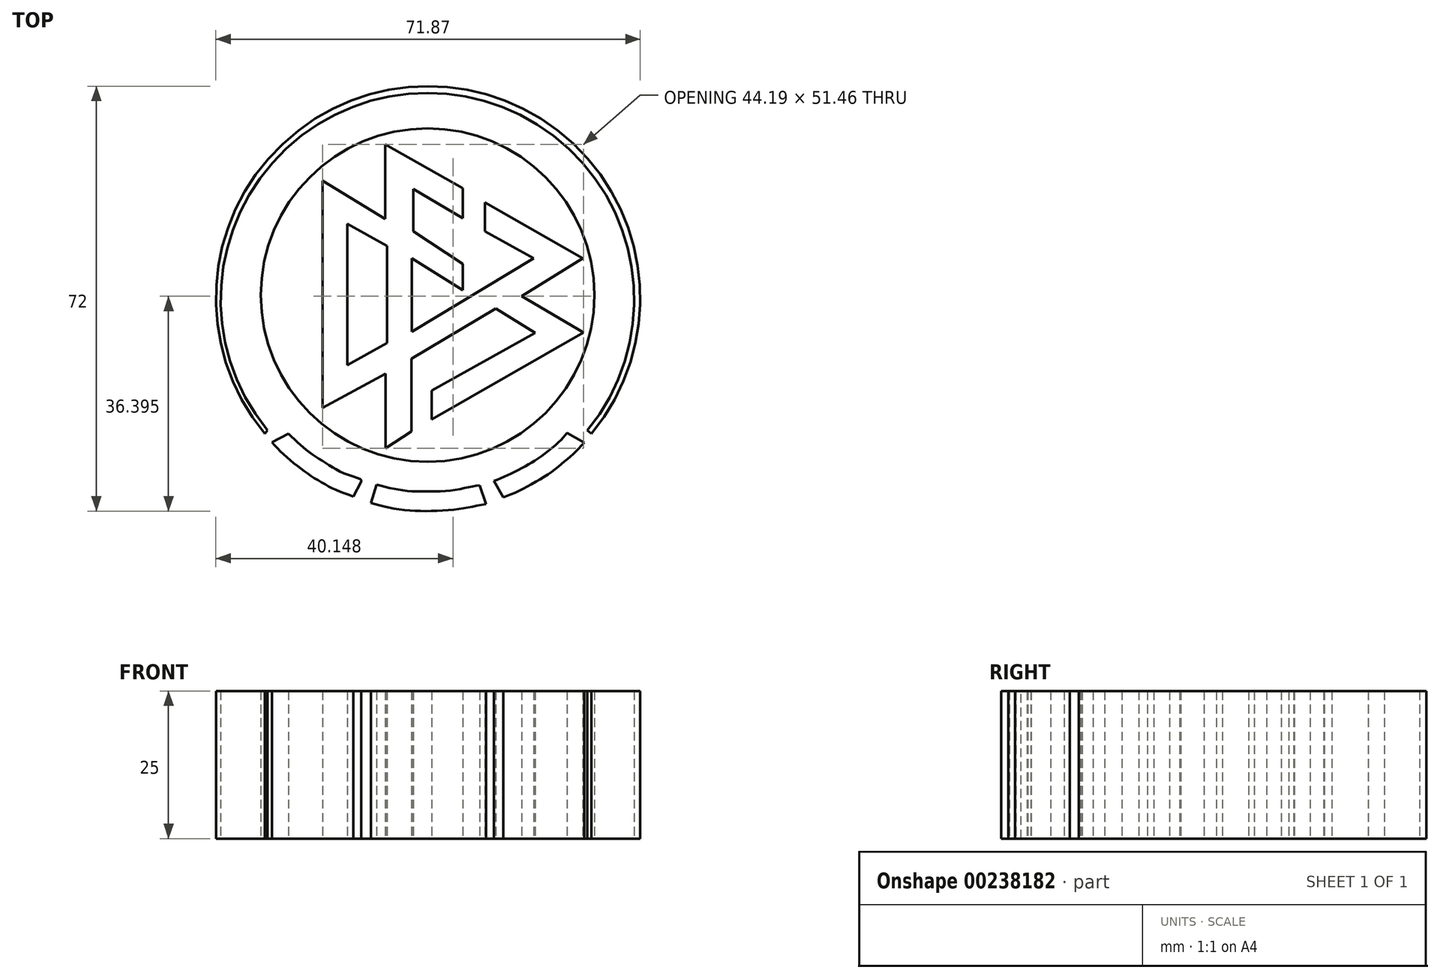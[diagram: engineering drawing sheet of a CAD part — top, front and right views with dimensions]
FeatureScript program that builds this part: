
annotation { "Feature Type Name" : "Feature", "Feature Type Description" : "" }
export const myFeature = defineFeature(function(context is Context, id is Id, definition is map)
    precondition{}
    {
        {
            var Q0;
            Q0=qCreatedBy(makeId("Top.planeOp"),FACE);
            var sketch = newSketch(context, id + "F0", { "sketchPlane" : qUnion([Q0])});
            skLineSegment(sketch, "E0", {"start": v(53.13, 37.91) * mm, "end": v(63.6, 31.78) * mm});
            skLineSegment(sketch, "E1", {"start": v(53.13, 37.91) * mm, "end": v(63.53, 44.34) * mm});
            skLineSegment(sketch, "E2", {"start": v(63.53, 44.34) * mm, "end": v(46.93, 53.84) * mm});
            skLineSegment(sketch, "E3", {"start": v(46.93, 53.84) * mm, "end": v(46.93, 48.9) * mm});
            skLineSegment(sketch, "E4", {"start": v(46.93, 48.9) * mm, "end": v(55.15, 44.34) * mm});
            skLineSegment(sketch, "E5", {"start": v(55.15, 44.34) * mm, "end": v(34.52, 31.9) * mm});
            skLineSegment(sketch, "E6", {"start": v(34.52, 31.9) * mm, "end": v(34.52, 44.34) * mm});
            skLineSegment(sketch, "E7", {"start": v(34.52, 44.34) * mm, "end": v(43.2, 38.96) * mm});
            skLineSegment(sketch, "E8", {"start": v(43.2, 38.96) * mm, "end": v(43.2, 43.37) * mm});
            skLineSegment(sketch, "E9", {"start": v(43.2, 43.37) * mm, "end": v(34.82, 48.9) * mm});
            skLineSegment(sketch, "E10", {"start": v(34.82, 48.9) * mm, "end": v(34.82, 56.08) * mm});
            skLineSegment(sketch, "E11", {"start": v(34.82, 56.08) * mm, "end": v(43.2, 51.15) * mm});
            skLineSegment(sketch, "E12", {"start": v(43.2, 51.15) * mm, "end": v(43.2, 56.23) * mm});
            skLineSegment(sketch, "E13", {"start": v(43.2, 56.23) * mm, "end": v(30.03, 63.63) * mm});
            skLineSegment(sketch, "E14", {"start": v(30.03, 63.63) * mm, "end": v(30.03, 51) * mm});
            skLineSegment(sketch, "E15", {"start": v(30.03, 51) * mm, "end": v(19.41, 57.5) * mm});
            skLineSegment(sketch, "E16", {"start": v(23.6, 50.17) * mm, "end": v(23.6, 26.25) * mm});
            skLineSegment(sketch, "E17", {"start": v(23.6, 26.25) * mm, "end": v(30.33, 29.99) * mm});
            skLineSegment(sketch, "E18", {"start": v(30.33, 29.99) * mm, "end": v(30.33, 46.44) * mm});
            skLineSegment(sketch, "E19", {"start": v(30.33, 46.44) * mm, "end": v(23.6, 50.17) * mm});
            skLineSegment(sketch, "E20", {"start": v(19.41, 57.5) * mm, "end": v(19.41, 19.03) * mm});
            skLineSegment(sketch, "E21", {"start": v(19.41, 19.03) * mm, "end": v(30.13, 24.76) * mm});
            skLineSegment(sketch, "E22", {"start": v(30.13, 24.76) * mm, "end": v(30.13, 12.18) * mm});
            skLineSegment(sketch, "E23", {"start": v(30.13, 12.18) * mm, "end": v(34.5, 15.03) * mm});
            skLineSegment(sketch, "E24", {"start": v(34.5, 15.03) * mm, "end": v(34.5, 27.3) * mm});
            skLineSegment(sketch, "E25", {"start": v(34.5, 27.3) * mm, "end": v(48.78, 35.83) * mm});
            skLineSegment(sketch, "E26", {"start": v(48.78, 35.83) * mm, "end": v(55.45, 31.74) * mm});
            skLineSegment(sketch, "E27", {"start": v(55.45, 31.74) * mm, "end": v(37.93, 21.9) * mm});
            skLineSegment(sketch, "E28", {"start": v(37.93, 21.9) * mm, "end": v(37.93, 17.02) * mm});
            skLineSegment(sketch, "E29", {"start": v(37.93, 17.02) * mm, "end": v(63.6, 31.78) * mm});
            skCircle(sketch, "E30", {"center": v(37.22, 38.12) * mm, "radius": 28.25 * mm});
            skPoint(sketch, "E30.centerSnap0", {"position": v(34.52, 38.12) * mm});
            skArc(sketch, "E31", {"start": v(64.3, 15.18) * mm, "mid": v(37.22, 72.37) * mm, "end": v(10.07, 15.21) * mm});
            skArc(sketch, "E32", {"start": v(64.98, 14.66) * mm, "mid": v(37.27, 73.5) * mm, "end": v(9.65, 14.61) * mm});
            skLineSegment(sketch, "E33", {"start": v(9.65, 14.61) * mm, "end": v(10.07, 15.21) * mm});
            skLineSegment(sketch, "E34", {"start": v(64.3, 15.18) * mm, "end": v(64.98, 14.66) * mm});
            skLineSegment(sketch, "E35", {"start": v(10.84, 13.16) * mm, "end": v(13.67, 14.61) * mm});
            skLineSegment(sketch, "E36", {"start": v(24.6, 3.99) * mm, "end": v(25.95, 6.53) * mm});
            skLineSegment(sketch, "E37", {"start": v(28.6, 5.96) * mm, "end": v(27.6, 2.9) * mm});
            skLineSegment(sketch, "E38", {"start": v(46.03, 5.9) * mm, "end": v(47.12, 2.72) * mm});
            skLineSegment(sketch, "E39", {"start": v(48.46, 6.6) * mm, "end": v(50.01, 3.84) * mm});
            skLineSegment(sketch, "E40", {"start": v(60.85, 14.78) * mm, "end": v(63.74, 13.13) * mm});
            skFitSpline(sketch, "E41", {"points": [v(10.84, 13.16) * mm, v(12.64, 11.3) * mm, v(15, 9.28) * mm, v(17.2, 7.66) * mm, v(19.42, 6.28) * mm, v(21.64, 5.12) * mm, v(24.6, 3.99) * mm], "startDerivative": vector(10.58, -11.57) * mm, "endDerivative": vector(17.38, -6.13) * mm});
            skFitSpline(sketch, "E42", {"points": [v(13.67, 14.61) * mm, v(15.82, 12.6) * mm, v(17.9, 10.97) * mm, v(20.44, 9.35) * mm, v(23.37, 7.8) * mm, v(25.95, 6.8) * mm, v(25.95, 6.53) * mm], "startDerivative": vector(11.45, -11.07) * mm, "endDerivative": vector(-1.87, -4.83) * mm});
            skFitSpline(sketch, "E43", {"points": [v(27.6, 2.9) * mm, v(30.08, 2.22) * mm, v(33.75, 1.66) * mm, v(37.38, 1.52) * mm, v(41.47, 1.73) * mm, v(44.44, 2.19) * mm, v(47.12, 2.72) * mm], "startDerivative": vector(15.75, -4.75) * mm, "endDerivative": vector(17.58, 3.54) * mm});
            skFitSpline(sketch, "E44", {"points": [v(28.6, 5.96) * mm, v(31.31, 5.33) * mm, v(34.2, 4.9) * mm, v(37.28, 4.83) * mm, v(40.95, 4.97) * mm, v(44.02, 5.5) * mm, v(46.03, 5.9) * mm], "startDerivative": vector(16.5, -4.12) * mm, "endDerivative": vector(13.71, 2.58) * mm});
            skFitSpline(sketch, "E45", {"points": [v(48.46, 6.6) * mm, v(50.97, 7.7) * mm, v(53.9, 9.17) * mm, v(56.4, 10.76) * mm, v(59.37, 13.16) * mm, v(60.85, 14.78) * mm], "startDerivative": vector(12.71, 5.37) * mm, "endDerivative": vector(7.5, 9) * mm});
            skFitSpline(sketch, "E46", {"points": [v(50.01, 3.84) * mm, v(52.52, 4.83) * mm, v(55.63, 6.53) * mm, v(58.41, 8.26) * mm, v(60.39, 9.91) * mm, v(62.01, 11.3) * mm, v(63.74, 13.13) * mm], "startDerivative": vector(15.05, 5.22) * mm, "endDerivative": vector(10.83, 12.2) * mm});
            skSolve(sketch);
        }
        {
            var Q0;
            Q0=makeQuery(id+"F0.imprint","IMPRINT",FACE,{"disambiguationData":[TD([[makeQuery(id+"F0.imprint","IMPRINT",EDGE,{"derivedFrom":sQuery(id+"F0.wireOp",EDGE,"E31")}),-1.0]])]});
            var Q1;
            Q1=makeQuery(id+"F0.imprint","IMPRINT",FACE,{"disambiguationData":[TD([[makeQuery(id+"F0.imprint","IMPRINT",EDGE,{"derivedFrom":sQuery(id+"F0.wireOp",EDGE,"E35")}),-1.0]])]});
            var Q2;
            Q2=makeQuery(id+"F0.imprint","IMPRINT",FACE,{"disambiguationData":[TD([[makeQuery(id+"F0.imprint","IMPRINT",EDGE,{"derivedFrom":sQuery(id+"F0.wireOp",EDGE,"E37")}),1.0]])]});
            var Q3;
            Q3=makeQuery(id+"F0.imprint","IMPRINT",FACE,{"disambiguationData":[TD([[makeQuery(id+"F0.imprint","IMPRINT",EDGE,{"derivedFrom":sQuery(id+"F0.wireOp",EDGE,"E39")}),1.0]])]});
            var Q4;
            Q4=makeQuery(id+"F0.imprint","IMPRINT",FACE,{"disambiguationData":[TD([[makeQuery(id+"F0.imprint","IMPRINT",EDGE,{"derivedFrom":sQuery(id+"F0.wireOp",EDGE,"E16")}),1.0]])]});
            var Q5;
            Q5=makeQuery(id+"F0.imprint","IMPRINT",FACE,{"disambiguationData":[TD([[makeQuery(id+"F0.imprint","IMPRINT",EDGE,{"derivedFrom":sQuery(id+"F0.wireOp",EDGE,"E0")}),1.0]])]});
            extrude(context, id + "F1", {"entities" : qUnion([Q0, Q1, Q2, Q3, Q4, Q5]), "depth" : 25 * mm});
        }
    });
